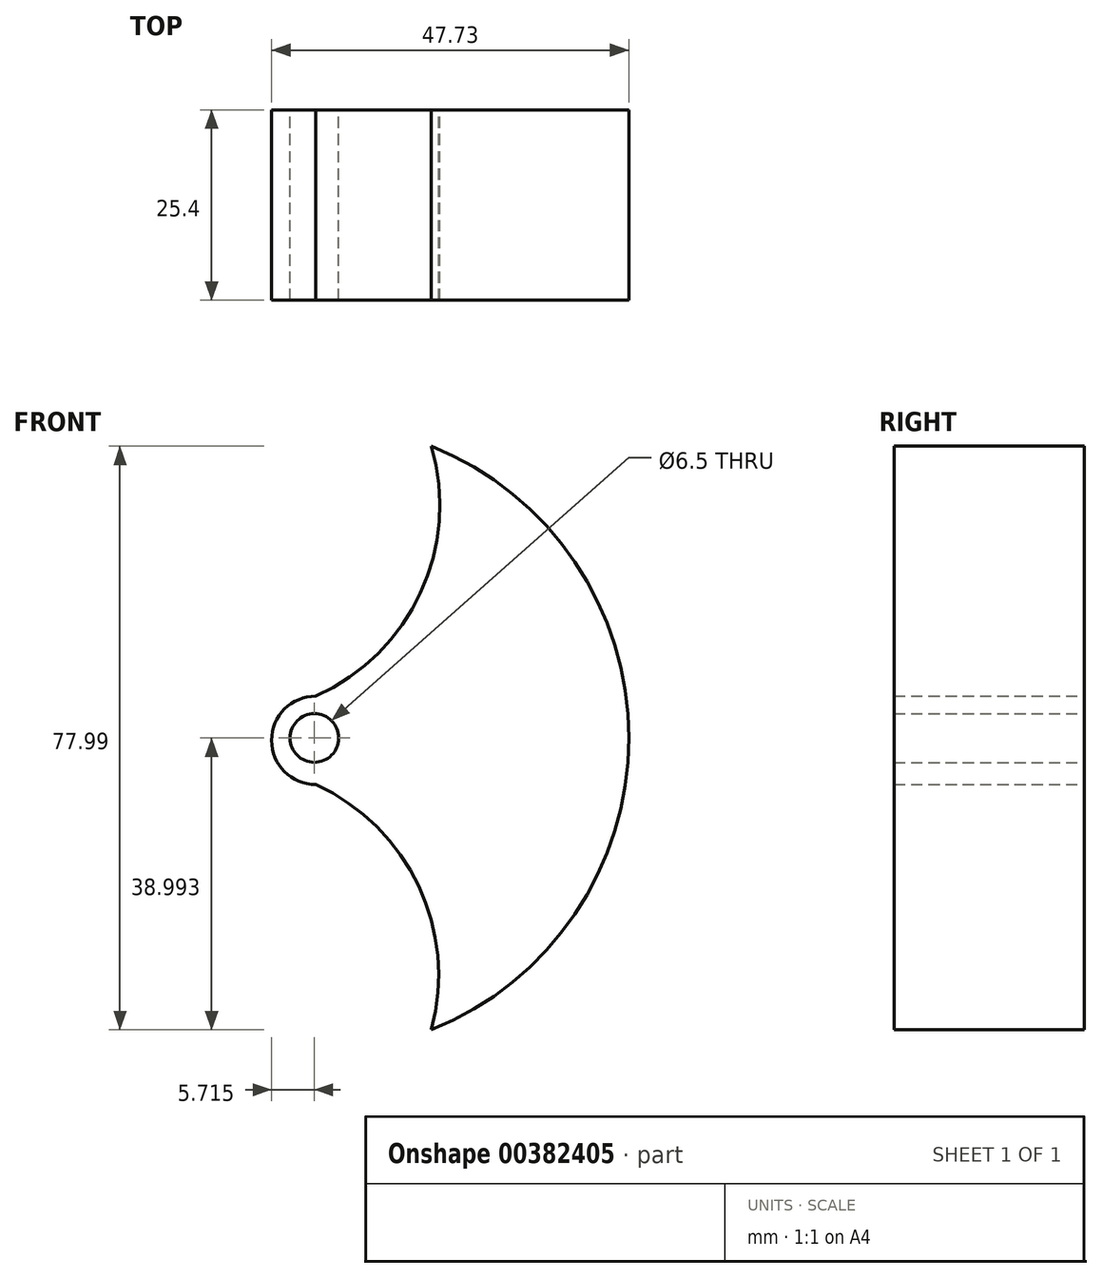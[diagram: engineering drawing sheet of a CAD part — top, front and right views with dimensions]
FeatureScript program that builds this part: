
annotation { "Feature Type Name" : "Feature", "Feature Type Description" : "" }
export const myFeature = defineFeature(function(context is Context, id is Id, definition is map)
    precondition{}
    {
        {
            var Q0;
            Q0=qCreatedBy(makeId("Front.planeOp"),FACE);
            var sketch = newSketch(context, id + "F0", { "sketchPlane" : qUnion([Q0])});
            skArc(sketch, "E0", {"start": v(0, 5.9) * mm, "mid": v(-5.9, 0) * mm, "end": v(0, -5.9) * mm});
            skArc(sketch, "E1", {"start": v(0, 5.9) * mm, "mid": v(13.98, 19.71) * mm, "end": v(15.44, 39.3) * mm});
            skArc(sketch, "E2", {"start": v(15.44, -38.68) * mm, "mid": v(13.74, -19.46) * mm, "end": v(0, -5.9) * mm});
            skArc(sketch, "E3", {"start": v(15.44, -38.68) * mm, "mid": v(41.82, 0.31) * mm, "end": v(15.44, 39.3) * mm});
            skCircle(sketch, "E4", {"center": v(-0.2, 0.31) * mm, "radius": 3.25 * mm});
            skSolve(sketch);
        }
        {
            var Q0;
            Q0=makeQuery(id+"F0.imprint","IMPRINT",FACE,{"disambiguationData":[TD([[makeQuery(id+"F0.imprint","IMPRINT",EDGE,{"derivedFrom":sQuery(id+"F0.wireOp",EDGE,"E0")}),1.0]])]});
            extrude(context, id + "F1", {"entities" : qUnion([Q0]), "depth" : 25.4 * mm});
        }
    });
